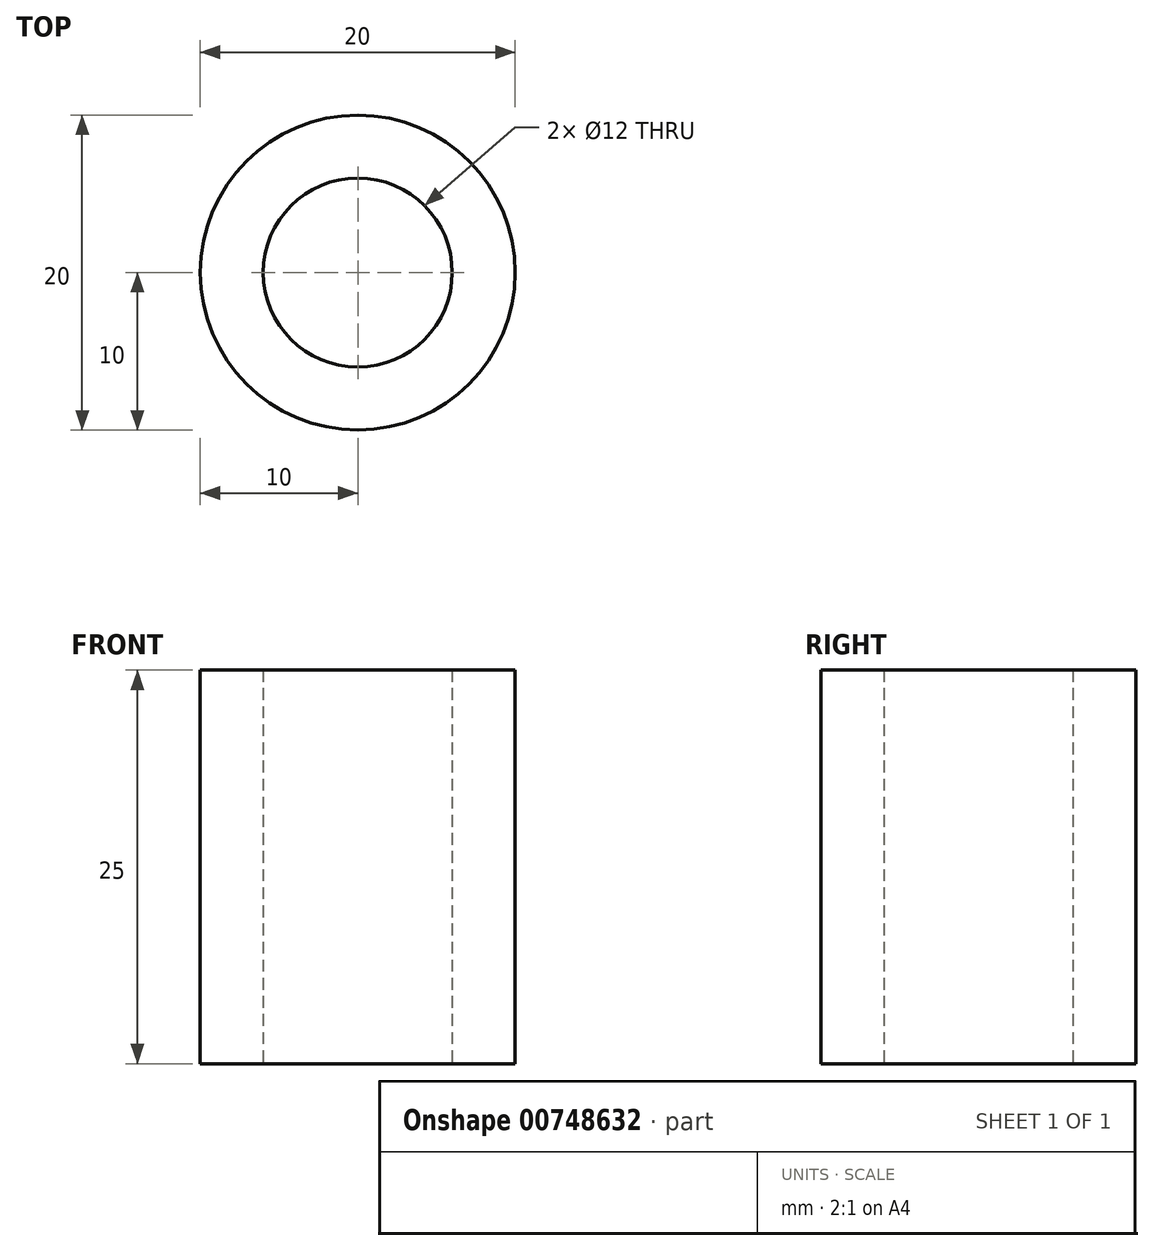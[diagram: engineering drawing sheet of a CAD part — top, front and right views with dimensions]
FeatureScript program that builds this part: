
annotation { "Feature Type Name" : "Feature", "Feature Type Description" : "" }
export const myFeature = defineFeature(function(context is Context, id is Id, definition is map)
    precondition{}
    {
        {
            var Q0;
            Q0=qCreatedBy(makeId("Top.planeOp"),FACE);
            var sketch = newSketch(context, id + "F0", { "sketchPlane" : qUnion([Q0])});
            skCircle(sketch, "E0", {"center": v(0, 0) * mm, "radius": 10 * mm});
            skCircle(sketch, "E1", {"center": v(0, 0) * mm, "radius": 6 * mm});
            skSolve(sketch);
        }
        {
            var Q0;
            Q0=makeQuery(id+"F0.imprint","IMPRINT",FACE,{"disambiguationData":[TD([[makeQuery(id+"F0.imprint","IMPRINT",EDGE,{"derivedFrom":sQuery(id+"F0.wireOp",EDGE,"E0")}),1.0]])]});
            extrude(context, id + "F1", {"entities" : qUnion([Q0]), "depth" : 25 * mm, "offsetDistance" : 25 * mm});
        }
    });
